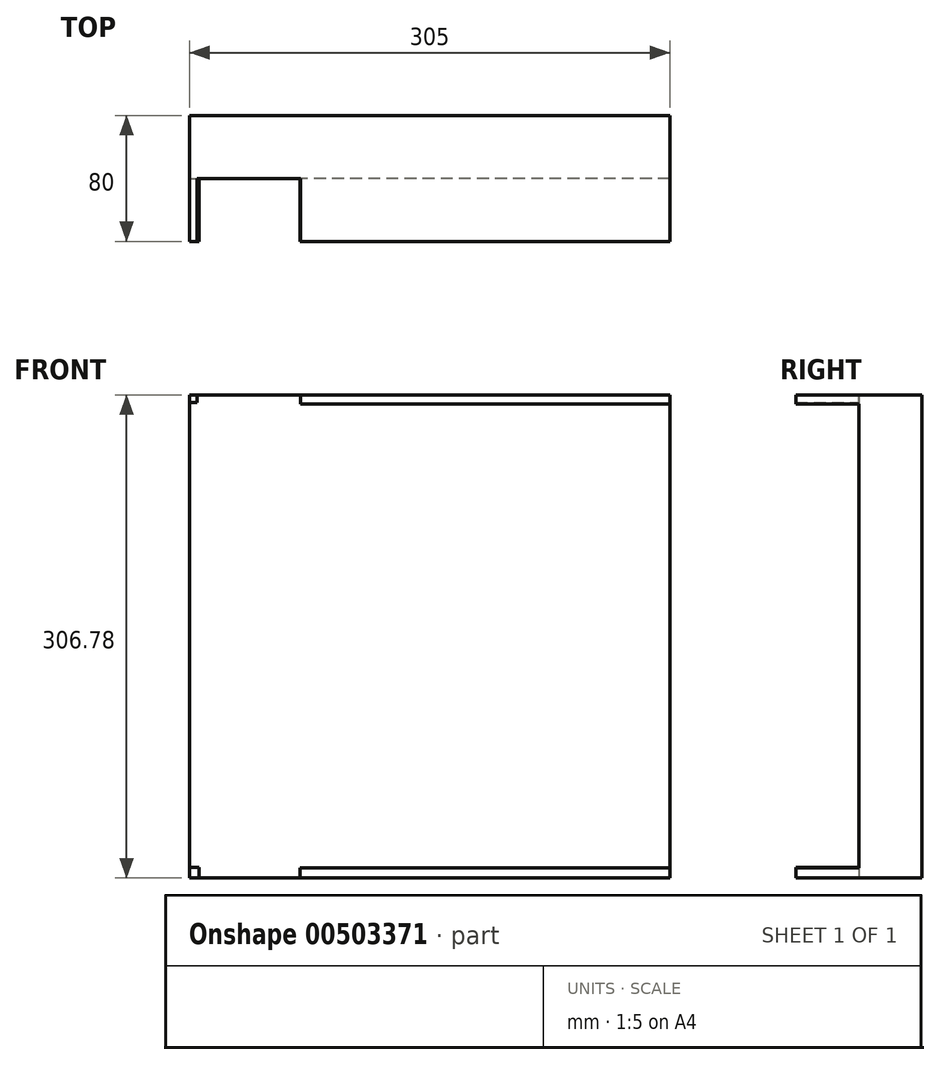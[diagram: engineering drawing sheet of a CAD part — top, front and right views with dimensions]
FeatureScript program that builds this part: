
annotation { "Feature Type Name" : "Feature", "Feature Type Description" : "" }
export const myFeature = defineFeature(function(context is Context, id is Id, definition is map)
    precondition{}
    {
        {
            var Q0;
            Q0=qCreatedBy(makeId("Front.planeOp"),FACE);
            var sketch = newSketch(context, id + "F0", { "sketchPlane" : qUnion([Q0])});
            skLineSegment(sketch, "E0.bottom", {"start": v(305, 306.78) * mm, "end": v(0, 306.78) * mm});
            skLineSegment(sketch, "E0.top", {"start": v(305, 0) * mm, "end": v(0, 0) * mm});
            skLineSegment(sketch, "E0.left", {"start": v(305, 306.78) * mm, "end": v(305, 0) * mm});
            skLineSegment(sketch, "E0.right", {"start": v(0, 306.78) * mm, "end": v(0, 0) * mm});
            skSolve(sketch);
        }
        {
            var Q0;
            Q0 = qSketchRegion(id + "F0", true);
            extrude(context, id + "F1", {"entities" : qUnion([Q0]), "depth" : 40 * mm});
        }
        {
            var Q0;
            Q0=makeQuery(id+"F1.opExtrude","CAP_FACE",FACE,{"disambiguationData":[OSD([sQuery(id+"F0.wireOp",EDGE,"E0.bottom"),sQuery(id+"F0.wireOp",EDGE,"E0.top"),sQuery(id+"F0.wireOp",EDGE,"E0.left"),sQuery(id+"F0.wireOp",EDGE,"E0.right")])],"isStart":false});
            var sketch = newSketch(context, id + "F2", { "sketchPlane" : qUnion([Q0])});
            skLineSegment(sketch, "E1.bottom", {"start": v(0, 306.78) * mm, "end": v(4.66, 306.78) * mm});
            skLineSegment(sketch, "E1.top", {"start": v(0, 301.94) * mm, "end": v(4.66, 301.94) * mm});
            skLineSegment(sketch, "E1.left", {"start": v(0, 306.78) * mm, "end": v(0, 301.94) * mm});
            skLineSegment(sketch, "E1.right", {"start": v(4.66, 306.78) * mm, "end": v(4.66, 301.94) * mm});
            skSolve(sketch);
        }
        {
            var Q0;
            Q0 = qSketchRegion(id + "F2", true);
            extrude(context, id + "F3", {"entities" : qUnion([Q0]), "operationType" : NewBodyOperationType.ADD, "depth" : 40 * mm});
        }
        {
            var Q0;
            Q0=makeQuery(id+"F1.opExtrude","CAP_FACE",FACE,{"disambiguationData":[OSD([sQuery(id+"F0.wireOp",EDGE,"E0.bottom"),sQuery(id+"F0.wireOp",EDGE,"E0.top"),sQuery(id+"F0.wireOp",EDGE,"E0.left"),sQuery(id+"F0.wireOp",EDGE,"E0.right")])],"isStart":false});
            var sketch = newSketch(context, id + "F4", { "sketchPlane" : qUnion([Q0])});
            skLineSegment(sketch, "E2.bottom", {"start": v(305, 301.09) * mm, "end": v(70.48, 301.09) * mm});
            skLineSegment(sketch, "E2.top", {"start": v(305, 306.78) * mm, "end": v(70.48, 306.78) * mm});
            skLineSegment(sketch, "E2.left", {"start": v(305, 301.09) * mm, "end": v(305, 306.78) * mm});
            skLineSegment(sketch, "E2.right", {"start": v(70.48, 301.09) * mm, "end": v(70.48, 306.78) * mm});
            skSolve(sketch);
        }
        {
            var Q0;
            Q0 = qSketchRegion(id + "F4", true);
            extrude(context, id + "F5", {"entities" : qUnion([Q0]), "operationType" : NewBodyOperationType.ADD, "depth" : 40 * mm});
        }
        {
            var Q0;
            Q0=makeQuery(id+"F1.opExtrude","CAP_FACE",FACE,{"disambiguationData":[OSD([sQuery(id+"F0.wireOp",EDGE,"E0.bottom"),sQuery(id+"F0.wireOp",EDGE,"E0.top"),sQuery(id+"F0.wireOp",EDGE,"E0.left"),sQuery(id+"F0.wireOp",EDGE,"E0.right")])],"isStart":false});
            var sketch = newSketch(context, id + "F6", { "sketchPlane" : qUnion([Q0])});
            skLineSegment(sketch, "E3.bottom", {"start": v(0, 6.8) * mm, "end": v(5.92, 6.8) * mm});
            skLineSegment(sketch, "E3.top", {"start": v(0, 0) * mm, "end": v(5.92, 0) * mm});
            skLineSegment(sketch, "E3.left", {"start": v(0, 6.8) * mm, "end": v(0, 0) * mm});
            skLineSegment(sketch, "E3.right", {"start": v(5.92, 6.8) * mm, "end": v(5.92, 0) * mm});
            skSolve(sketch);
        }
        {
            var Q0;
            Q0 = qSketchRegion(id + "F6", true);
            extrude(context, id + "F7", {"entities" : qUnion([Q0]), "operationType" : NewBodyOperationType.ADD, "depth" : 40 * mm});
        }
        {
            var Q0;
            Q0=makeQuery(id+"F1.opExtrude","CAP_FACE",FACE,{"disambiguationData":[OSD([sQuery(id+"F0.wireOp",EDGE,"E0.bottom"),sQuery(id+"F0.wireOp",EDGE,"E0.top"),sQuery(id+"F0.wireOp",EDGE,"E0.left"),sQuery(id+"F0.wireOp",EDGE,"E0.right")])],"isStart":false});
            var sketch = newSketch(context, id + "F8", { "sketchPlane" : qUnion([Q0])});
            skLineSegment(sketch, "E4.bottom", {"start": v(305, 6.33) * mm, "end": v(70.1, 6.33) * mm});
            skLineSegment(sketch, "E4.top", {"start": v(305, 0) * mm, "end": v(70.1, 0) * mm});
            skLineSegment(sketch, "E4.left", {"start": v(305, 6.33) * mm, "end": v(305, 0) * mm});
            skLineSegment(sketch, "E4.right", {"start": v(70.1, 6.33) * mm, "end": v(70.1, 0) * mm});
            skSolve(sketch);
        }
        {
            var Q0;
            Q0 = qSketchRegion(id + "F8", true);
            extrude(context, id + "F9", {"entities" : qUnion([Q0]), "operationType" : NewBodyOperationType.ADD, "depth" : 40 * mm});
        }
    });
